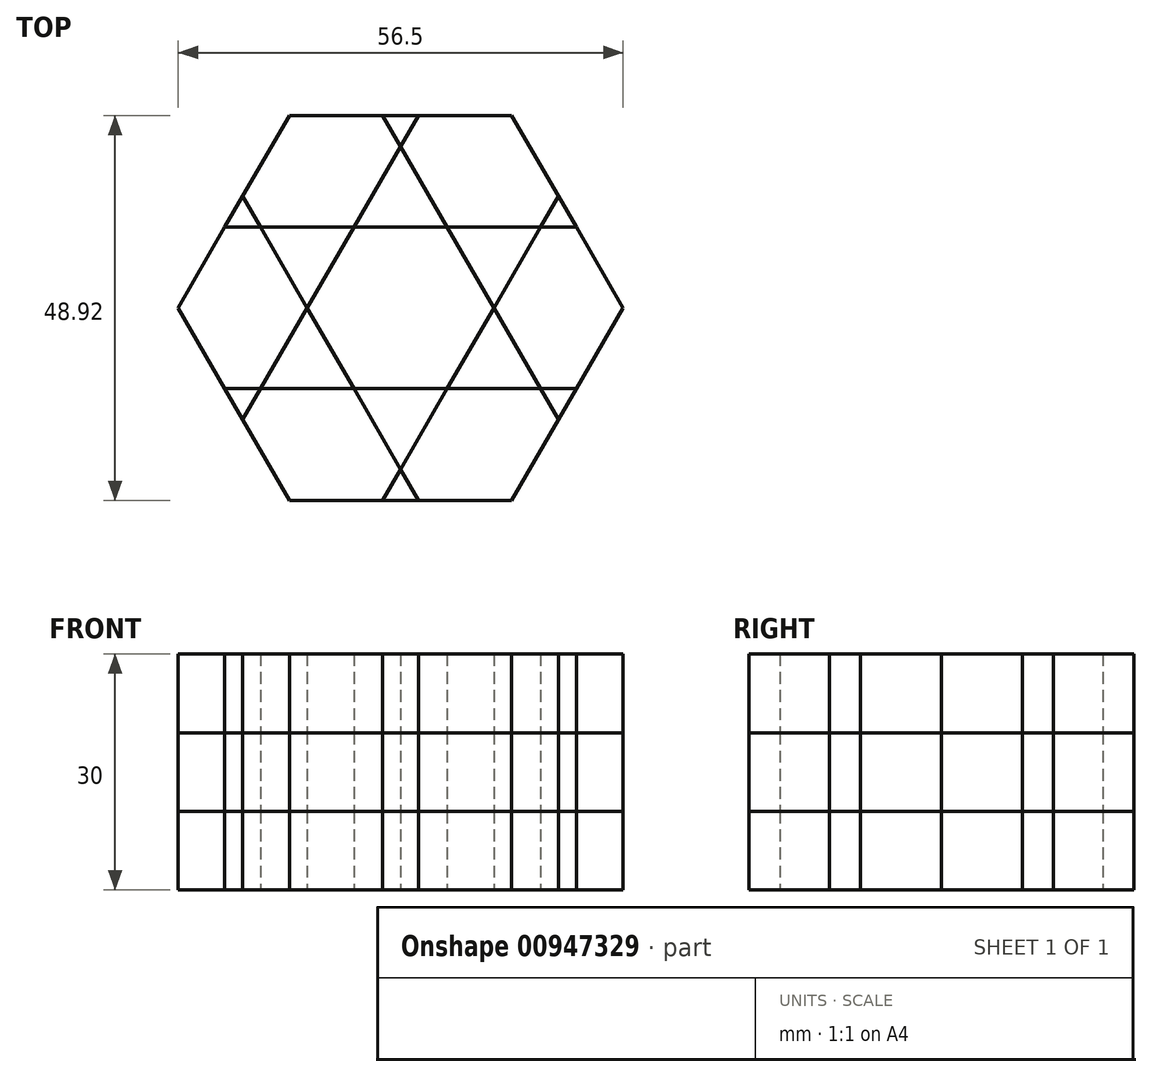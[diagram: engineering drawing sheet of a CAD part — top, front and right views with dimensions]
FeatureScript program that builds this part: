
annotation { "Feature Type Name" : "Feature", "Feature Type Description" : "" }
export const myFeature = defineFeature(function(context is Context, id is Id, definition is map)
    precondition{}
    {
        {
            var Q0;
            Q0=qCreatedBy(makeId("Top.planeOp"),FACE);
            var sketch = newSketch(context, id + "F0", { "sketchPlane" : qUnion([Q0])});
            skCircle(sketch, "E0.cCircle", {"center": v(0, 0) * mm, "radius": 10.26 * mm, "construction": true});
            skLineSegment(sketch, "E0.0", {"start": v(-5.92, 10.26) * mm, "end": v(5.92, 10.26) * mm});
            skLineSegment(sketch, "E0.1", {"start": v(5.92, 10.26) * mm, "end": v(11.85, 0) * mm});
            skLineSegment(sketch, "E0.2", {"start": v(11.85, 0) * mm, "end": v(5.92, -10.26) * mm});
            skLineSegment(sketch, "E0.3", {"start": v(5.92, -10.26) * mm, "end": v(-5.92, -10.26) * mm});
            skLineSegment(sketch, "E0.4", {"start": v(-5.92, -10.26) * mm, "end": v(-11.85, 0) * mm});
            skLineSegment(sketch, "E0.5", {"start": v(-11.85, 0) * mm, "end": v(-5.92, 10.26) * mm});
            skPoint(sketch, "E0.0.midPoint", {"position": v(0, 10.26) * mm});
            skCircle(sketch, "E1.cCircle", {"center": v(0, 0) * mm, "radius": 24.46 * mm, "construction": true});
            skLineSegment(sketch, "E1.0", {"start": v(-14.12, 24.46) * mm, "end": v(14.12, 24.46) * mm});
            skLineSegment(sketch, "E1.1", {"start": v(14.12, 24.46) * mm, "end": v(28.25, 0) * mm});
            skLineSegment(sketch, "E1.2", {"start": v(28.25, 0) * mm, "end": v(14.12, -24.46) * mm});
            skLineSegment(sketch, "E1.3", {"start": v(14.12, -24.46) * mm, "end": v(-14.12, -24.46) * mm});
            skLineSegment(sketch, "E1.4", {"start": v(-14.12, -24.46) * mm, "end": v(-28.25, 0) * mm});
            skLineSegment(sketch, "E1.5", {"start": v(-28.25, 0) * mm, "end": v(-14.12, 24.46) * mm});
            skPoint(sketch, "E1.0.midPoint", {"position": v(0, 24.46) * mm});
            skLineSegment(sketch, "E2", {"start": v(5.92, 10.26) * mm, "end": v(-2.28, 24.46) * mm});
            skLineSegment(sketch, "E3", {"start": v(5.92, -10.26) * mm, "end": v(22.32, -10.26) * mm});
            skLineSegment(sketch, "E4", {"start": v(11.85, 0) * mm, "end": v(20.05, 14.2) * mm});
            skLineSegment(sketch, "E5", {"start": v(-5.92, 10.26) * mm, "end": v(22.32, 10.26) * mm});
            skLineSegment(sketch, "E6", {"start": v(-5.92, 10.26) * mm, "end": v(-22.32, 10.26) * mm});
            skLineSegment(sketch, "E7", {"start": v(-5.92, 10.26) * mm, "end": v(2.28, 24.46) * mm});
            skLineSegment(sketch, "E8", {"start": v(-11.85, 0) * mm, "end": v(-20.05, 14.2) * mm});
            skLineSegment(sketch, "E9", {"start": v(-11.85, 0) * mm, "end": v(-20.05, -14.2) * mm});
            skLineSegment(sketch, "E10", {"start": v(-5.92, -10.26) * mm, "end": v(-22.32, -10.26) * mm});
            skLineSegment(sketch, "E11", {"start": v(5.92, -10.26) * mm, "end": v(-2.28, -24.46) * mm});
            skLineSegment(sketch, "E12", {"start": v(-5.92, -10.26) * mm, "end": v(2.28, -24.46) * mm});
            skLineSegment(sketch, "E13", {"start": v(11.85, 0) * mm, "end": v(20.05, -14.2) * mm});
            skSolve(sketch);
        }
        {
            var Q0;
            {var subQ5=sQuery(id+"F0.wireOp",EDGE,"E1.5");var subQ6=sQuery(id+"F0.wireOp",EDGE,"E1.0");var subQ7=makeQuery(id+"F0.imprint","INTERSECT",VERTEX,{"derivedFrom":[subQ6,subQ5]});Q0=makeQuery(id+"F0.imprint","IMPRINT",FACE,{"disambiguationData":[TD([[makeQuery(id+"F0.imprint","IMPRINT",EDGE,{"disambiguationData":[TD([[subQ7,-1.0]])],"derivedFrom":subQ6}),-1.0]])]});}
            var Q1;
            {var subQ0=sQuery(id+"F0.wireOp",EDGE,"E1.1");var subQ1=sQuery(id+"F0.wireOp",EDGE,"E1.0");var subQ2=makeQuery(id+"F0.imprint","INTERSECT",VERTEX,{"derivedFrom":[subQ1,subQ0]});Q1=makeQuery(id+"F0.imprint","IMPRINT",FACE,{"disambiguationData":[TD([[makeQuery(id+"F0.imprint","IMPRINT",EDGE,{"disambiguationData":[TD([[subQ2,1.0]])],"derivedFrom":subQ1}),-1.0]])]});}
            var Q2;
            {var subQ5=sQuery(id+"F0.wireOp",EDGE,"E1.2");var subQ6=sQuery(id+"F0.wireOp",EDGE,"E1.1");var subQ7=makeQuery(id+"F0.imprint","INTERSECT",VERTEX,{"derivedFrom":[subQ6,subQ5]});Q2=makeQuery(id+"F0.imprint","IMPRINT",FACE,{"disambiguationData":[TD([[makeQuery(id+"F0.imprint","IMPRINT",EDGE,{"disambiguationData":[TD([[subQ7,1.0]])],"derivedFrom":subQ6}),-1.0]])]});}
            var Q3;
            {var subQ1=sQuery(id+"F0.wireOp",EDGE,"E1.4");var subQ5=sQuery(id+"F0.wireOp",EDGE,"E1.3");var subQ6=makeQuery(id+"F0.imprint","INTERSECT",VERTEX,{"derivedFrom":[subQ5,subQ1]});Q3=makeQuery(id+"F0.imprint","IMPRINT",FACE,{"disambiguationData":[TD([[makeQuery(id+"F0.imprint","IMPRINT",EDGE,{"disambiguationData":[TD([[subQ6,1.0]])],"derivedFrom":subQ5}),-1.0]])]});}
            var Q4;
            {var subQ5=sQuery(id+"F0.wireOp",EDGE,"E1.5");var subQ6=sQuery(id+"F0.wireOp",EDGE,"E1.4");var subQ7=makeQuery(id+"F0.imprint","INTERSECT",VERTEX,{"derivedFrom":[subQ6,subQ5]});Q4=makeQuery(id+"F0.imprint","IMPRINT",FACE,{"disambiguationData":[TD([[makeQuery(id+"F0.imprint","IMPRINT",EDGE,{"disambiguationData":[TD([[subQ7,1.0]])],"derivedFrom":subQ6}),-1.0]])]});}
            var Q5;
            {var subQ7=sQuery(id+"F0.wireOp",EDGE,"E1.3");var subQ8=sQuery(id+"F0.wireOp",EDGE,"E1.2");var subQ9=makeQuery(id+"F0.imprint","INTERSECT",VERTEX,{"derivedFrom":[subQ8,subQ7]});Q5=makeQuery(id+"F0.imprint","IMPRINT",FACE,{"disambiguationData":[TD([[makeQuery(id+"F0.imprint","IMPRINT",EDGE,{"disambiguationData":[TD([[subQ9,1.0]])],"derivedFrom":subQ8}),-1.0]])]});}
            var Q6;
            {var subQ0=sQuery(id+"F0.wireOp",EDGE,"E0.1");Q6=makeQuery(id+"F0.imprint","IMPRINT",FACE,{"disambiguationData":[TD([[makeQuery(id+"F0.imprint","IMPRINT",EDGE,{"derivedFrom":subQ0}),-1.0]])]});}
            extrude(context, id + "F1", {"entities" : qUnion([Q0, Q1, Q2, Q3, Q4, Q5, Q6]), "depth" : 10 * mm, "offsetDistance" : 25.4 * mm});
        }
        {
            var Q0;
            {var subQ0=sQuery(id+"F0.wireOp",EDGE,"E6");var subQ1=sQuery(id+"F0.wireOp",EDGE,"E1.5");var subQ2=makeQuery(id+"F0.imprint","INTERSECT",VERTEX,{"derivedFrom":[subQ1,subQ0]});Q0=makeQuery(id+"F0.imprint","IMPRINT",FACE,{"disambiguationData":[TD([[makeQuery(id+"F0.imprint","IMPRINT",EDGE,{"disambiguationData":[TD([[subQ2,-1.0]])],"derivedFrom":subQ1}),-1.0]])]});}
            var Q1;
            {var subQ0=sQuery(id+"F0.wireOp",EDGE,"E0.5");Q1=makeQuery(id+"F0.imprint","IMPRINT",FACE,{"disambiguationData":[TD([[makeQuery(id+"F0.imprint","IMPRINT",EDGE,{"derivedFrom":subQ0}),1.0]])]});}
            var Q2;
            {var subQ0=sQuery(id+"F0.wireOp",EDGE,"E2");var subQ1=sQuery(id+"F0.wireOp",EDGE,"E1.0");var subQ2=makeQuery(id+"F0.imprint","INTERSECT",VERTEX,{"derivedFrom":[subQ1,subQ0]});Q2=makeQuery(id+"F0.imprint","IMPRINT",FACE,{"disambiguationData":[TD([[makeQuery(id+"F0.imprint","IMPRINT",EDGE,{"disambiguationData":[TD([[subQ2,-1.0]])],"derivedFrom":subQ1}),-1.0]])]});}
            var Q3;
            {var subQ1=sQuery(id+"F0.wireOp",EDGE,"E2");var subQ3=sQuery(id+"F0.wireOp",EDGE,"E7");var subQ4=makeQuery(id+"F0.imprint","INTERSECT",VERTEX,{"derivedFrom":[subQ1,subQ3]});Q3=makeQuery(id+"F0.imprint","IMPRINT",FACE,{"disambiguationData":[TD([[makeQuery(id+"F0.imprint","IMPRINT",EDGE,{"disambiguationData":[TD([[subQ4,1.0]])],"derivedFrom":subQ1}),1.0]])]});}
            var Q4;
            {var subQ0=sQuery(id+"F0.wireOp",EDGE,"E0.1");Q4=makeQuery(id+"F0.imprint","IMPRINT",FACE,{"disambiguationData":[TD([[makeQuery(id+"F0.imprint","IMPRINT",EDGE,{"derivedFrom":subQ0}),1.0]])]});}
            var Q5;
            {var subQ0=sQuery(id+"F0.wireOp",EDGE,"E4");var subQ1=sQuery(id+"F0.wireOp",EDGE,"E1.1");var subQ2=makeQuery(id+"F0.imprint","INTERSECT",VERTEX,{"derivedFrom":[subQ1,subQ0]});Q5=makeQuery(id+"F0.imprint","IMPRINT",FACE,{"disambiguationData":[TD([[makeQuery(id+"F0.imprint","IMPRINT",EDGE,{"disambiguationData":[TD([[subQ2,-1.0]])],"derivedFrom":subQ1}),-1.0]])]});}
            var Q6;
            {var subQ0=sQuery(id+"F0.wireOp",EDGE,"E0.2");Q6=makeQuery(id+"F0.imprint","IMPRINT",FACE,{"disambiguationData":[TD([[makeQuery(id+"F0.imprint","IMPRINT",EDGE,{"derivedFrom":subQ0}),1.0]])]});}
            var Q7;
            {var subQ0=sQuery(id+"F0.wireOp",EDGE,"E3");var subQ1=sQuery(id+"F0.wireOp",EDGE,"E1.2");var subQ2=makeQuery(id+"F0.imprint","INTERSECT",VERTEX,{"derivedFrom":[subQ1,subQ0]});Q7=makeQuery(id+"F0.imprint","IMPRINT",FACE,{"disambiguationData":[TD([[makeQuery(id+"F0.imprint","IMPRINT",EDGE,{"disambiguationData":[TD([[subQ2,-1.0]])],"derivedFrom":subQ1}),-1.0]])]});}
            var Q8;
            {var subQ0=sQuery(id+"F0.wireOp",EDGE,"E0.3");Q8=makeQuery(id+"F0.imprint","IMPRINT",FACE,{"disambiguationData":[TD([[makeQuery(id+"F0.imprint","IMPRINT",EDGE,{"derivedFrom":subQ0}),1.0]])]});}
            var Q9;
            {var subQ0=sQuery(id+"F0.wireOp",EDGE,"E0.4");Q9=makeQuery(id+"F0.imprint","IMPRINT",FACE,{"disambiguationData":[TD([[makeQuery(id+"F0.imprint","IMPRINT",EDGE,{"derivedFrom":subQ0}),1.0]])]});}
            var Q10;
            {var subQ0=sQuery(id+"F0.wireOp",EDGE,"E9");var subQ1=sQuery(id+"F0.wireOp",EDGE,"E1.4");var subQ2=makeQuery(id+"F0.imprint","INTERSECT",VERTEX,{"derivedFrom":[subQ1,subQ0]});Q10=makeQuery(id+"F0.imprint","IMPRINT",FACE,{"disambiguationData":[TD([[makeQuery(id+"F0.imprint","IMPRINT",EDGE,{"disambiguationData":[TD([[subQ2,-1.0]])],"derivedFrom":subQ1}),-1.0]])]});}
            var Q11;
            {var subQ0=sQuery(id+"F0.wireOp",EDGE,"E11");var subQ1=sQuery(id+"F0.wireOp",EDGE,"E1.3");var subQ2=makeQuery(id+"F0.imprint","INTERSECT",VERTEX,{"derivedFrom":[subQ1,subQ0]});Q11=makeQuery(id+"F0.imprint","IMPRINT",FACE,{"disambiguationData":[TD([[makeQuery(id+"F0.imprint","IMPRINT",EDGE,{"disambiguationData":[TD([[subQ2,1.0]])],"derivedFrom":subQ1}),-1.0]])]});}
            extrude(context, id + "F2", {"entities" : qUnion([Q0, Q1, Q2, Q3, Q4, Q5, Q6, Q7, Q8, Q9, Q10, Q11]), "depth" : 10 * mm, "offsetDistance" : 25.4 * mm});
        }
        {
            var Q0;
            Q0=makeQuery(id+"F1.opExtrude","SWEPT_BODY",BODY,{"disambiguationData":[OSD([sQuery(id+"F0.wireOp",EDGE,"E1.0"),sQuery(id+"F0.wireOp",EDGE,"E1.5"),sQuery(id+"F0.wireOp",EDGE,"E2"),sQuery(id+"F0.wireOp",EDGE,"E6"),sQuery(id+"F0.wireOp",EDGE,"E7"),sQuery(id+"F0.wireOp",EDGE,"E8")])]});
            var Q1;
            Q1=makeQuery(id+"F1.opExtrude","SWEPT_BODY",BODY,{"disambiguationData":[OSD([sQuery(id+"F0.wireOp",EDGE,"E1.0"),sQuery(id+"F0.wireOp",EDGE,"E1.1"),sQuery(id+"F0.wireOp",EDGE,"E2"),sQuery(id+"F0.wireOp",EDGE,"E4"),sQuery(id+"F0.wireOp",EDGE,"E5"),sQuery(id+"F0.wireOp",EDGE,"E7")])]});
            var Q2;
            Q2=makeQuery(id+"F1.opExtrude","SWEPT_BODY",BODY,{"disambiguationData":[OSD([sQuery(id+"F0.wireOp",EDGE,"E1.1"),sQuery(id+"F0.wireOp",EDGE,"E1.2"),sQuery(id+"F0.wireOp",EDGE,"E3"),sQuery(id+"F0.wireOp",EDGE,"E4"),sQuery(id+"F0.wireOp",EDGE,"E5"),sQuery(id+"F0.wireOp",EDGE,"E13")])]});
            var Q3;
            Q3=makeQuery(id+"F1.opExtrude","SWEPT_BODY",BODY,{"disambiguationData":[OSD([sQuery(id+"F0.wireOp",EDGE,"E1.2"),sQuery(id+"F0.wireOp",EDGE,"E1.3"),sQuery(id+"F0.wireOp",EDGE,"E3"),sQuery(id+"F0.wireOp",EDGE,"E11"),sQuery(id+"F0.wireOp",EDGE,"E12"),sQuery(id+"F0.wireOp",EDGE,"E13")])]});
            var Q4;
            Q4=makeQuery(id+"F1.opExtrude","SWEPT_BODY",BODY,{"disambiguationData":[OSD([sQuery(id+"F0.wireOp",EDGE,"E1.3"),sQuery(id+"F0.wireOp",EDGE,"E1.4"),sQuery(id+"F0.wireOp",EDGE,"E9"),sQuery(id+"F0.wireOp",EDGE,"E10"),sQuery(id+"F0.wireOp",EDGE,"E11"),sQuery(id+"F0.wireOp",EDGE,"E12")])]});
            var Q5;
            Q5=makeQuery(id+"F1.opExtrude","SWEPT_BODY",BODY,{"disambiguationData":[OSD([sQuery(id+"F0.wireOp",EDGE,"E1.4"),sQuery(id+"F0.wireOp",EDGE,"E1.5"),sQuery(id+"F0.wireOp",EDGE,"E6"),sQuery(id+"F0.wireOp",EDGE,"E8"),sQuery(id+"F0.wireOp",EDGE,"E9"),sQuery(id+"F0.wireOp",EDGE,"E10")])]});
            var Q6;
            Q6=makeQuery(id+"F2.opExtrude","SWEPT_BODY",BODY,{"disambiguationData":[OSD([sQuery(id+"F0.wireOp",EDGE,"E0.1"),sQuery(id+"F0.wireOp",EDGE,"E4"),sQuery(id+"F0.wireOp",EDGE,"E5")])]});
            var Q7;
            Q7=makeQuery(id+"F2.opExtrude","SWEPT_BODY",BODY,{"disambiguationData":[OSD([sQuery(id+"F0.wireOp",EDGE,"E0.2"),sQuery(id+"F0.wireOp",EDGE,"E3"),sQuery(id+"F0.wireOp",EDGE,"E13")])]});
            var Q8;
            Q8=makeQuery(id+"F2.opExtrude","SWEPT_BODY",BODY,{"disambiguationData":[OSD([sQuery(id+"F0.wireOp",EDGE,"E0.3"),sQuery(id+"F0.wireOp",EDGE,"E11"),sQuery(id+"F0.wireOp",EDGE,"E12")])]});
            var Q9;
            Q9=makeQuery(id+"F2.opExtrude","SWEPT_BODY",BODY,{"disambiguationData":[OSD([sQuery(id+"F0.wireOp",EDGE,"E0.4"),sQuery(id+"F0.wireOp",EDGE,"E9"),sQuery(id+"F0.wireOp",EDGE,"E10")])]});
            var Q10;
            Q10=makeQuery(id+"F2.opExtrude","SWEPT_BODY",BODY,{"disambiguationData":[OSD([sQuery(id+"F0.wireOp",EDGE,"E0.5"),sQuery(id+"F0.wireOp",EDGE,"E6"),sQuery(id+"F0.wireOp",EDGE,"E8")])]});
            var Q11;
            Q11=makeQuery(id+"F2.opExtrude","SWEPT_BODY",BODY,{"disambiguationData":[OSD([sQuery(id+"F0.wireOp",EDGE,"E1.0"),sQuery(id+"F0.wireOp",EDGE,"E2"),sQuery(id+"F0.wireOp",EDGE,"E7")])]});
            var Q12;
            Q12=makeQuery(id+"F2.opExtrude","SWEPT_BODY",BODY,{"disambiguationData":[OSD([sQuery(id+"F0.wireOp",EDGE,"E1.1"),sQuery(id+"F0.wireOp",EDGE,"E4"),sQuery(id+"F0.wireOp",EDGE,"E5")])]});
            var Q13;
            Q13=makeQuery(id+"F2.opExtrude","SWEPT_BODY",BODY,{"disambiguationData":[OSD([sQuery(id+"F0.wireOp",EDGE,"E1.2"),sQuery(id+"F0.wireOp",EDGE,"E3"),sQuery(id+"F0.wireOp",EDGE,"E13")])]});
            var Q14;
            Q14=makeQuery(id+"F2.opExtrude","SWEPT_BODY",BODY,{"disambiguationData":[OSD([sQuery(id+"F0.wireOp",EDGE,"E1.3"),sQuery(id+"F0.wireOp",EDGE,"E11"),sQuery(id+"F0.wireOp",EDGE,"E12")])]});
            var Q15;
            Q15=makeQuery(id+"F2.opExtrude","SWEPT_BODY",BODY,{"disambiguationData":[OSD([sQuery(id+"F0.wireOp",EDGE,"E1.4"),sQuery(id+"F0.wireOp",EDGE,"E9"),sQuery(id+"F0.wireOp",EDGE,"E10")])]});
            var Q16;
            Q16=makeQuery(id+"F2.opExtrude","SWEPT_BODY",BODY,{"disambiguationData":[OSD([sQuery(id+"F0.wireOp",EDGE,"E1.5"),sQuery(id+"F0.wireOp",EDGE,"E6"),sQuery(id+"F0.wireOp",EDGE,"E8")])]});
            var Q17;
            Q17=makeQuery(id+"F2.opExtrude","SWEPT_BODY",BODY,{"disambiguationData":[OSD([sQuery(id+"F0.wireOp",EDGE,"E2"),sQuery(id+"F0.wireOp",EDGE,"E5"),sQuery(id+"F0.wireOp",EDGE,"E7")])]});
            var Q18;
            Q18=makeQuery(id+"F1.opExtrude","SWEPT_BODY",BODY,{"disambiguationData":[OSD([sQuery(id+"F0.wireOp",EDGE,"E0.1"),sQuery(id+"F0.wireOp",EDGE,"E0.2"),sQuery(id+"F0.wireOp",EDGE,"E0.3"),sQuery(id+"F0.wireOp",EDGE,"E0.4"),sQuery(id+"F0.wireOp",EDGE,"E0.5"),sQuery(id+"F0.wireOp",EDGE,"E5")])]});
            transform(context, id + "F3", {"entities" : qUnion([Q0, Q1, Q2, Q3, Q4, Q5, Q6, Q7, Q8, Q9, Q10, Q11, Q12, Q13, Q14, Q15, Q16, Q17, Q18]), "transformType" : TransformType.TRANSLATION_3D, "dx" : 0 * mm, "dy" : 0 * mm, "dz" : 10 * mm, "makeCopy" : true});
        }
        {
            var Q0;
            Q0=makeQuery(id+"F1.opExtrude","SWEPT_BODY",BODY,{"disambiguationData":[OSD([sQuery(id+"F0.wireOp",EDGE,"E1.0"),sQuery(id+"F0.wireOp",EDGE,"E1.5"),sQuery(id+"F0.wireOp",EDGE,"E2"),sQuery(id+"F0.wireOp",EDGE,"E6"),sQuery(id+"F0.wireOp",EDGE,"E7"),sQuery(id+"F0.wireOp",EDGE,"E8")])]});
            var Q1;
            Q1=makeQuery(id+"F1.opExtrude","SWEPT_BODY",BODY,{"disambiguationData":[OSD([sQuery(id+"F0.wireOp",EDGE,"E1.0"),sQuery(id+"F0.wireOp",EDGE,"E1.1"),sQuery(id+"F0.wireOp",EDGE,"E2"),sQuery(id+"F0.wireOp",EDGE,"E4"),sQuery(id+"F0.wireOp",EDGE,"E5"),sQuery(id+"F0.wireOp",EDGE,"E7")])]});
            var Q2;
            Q2=makeQuery(id+"F1.opExtrude","SWEPT_BODY",BODY,{"disambiguationData":[OSD([sQuery(id+"F0.wireOp",EDGE,"E1.1"),sQuery(id+"F0.wireOp",EDGE,"E1.2"),sQuery(id+"F0.wireOp",EDGE,"E3"),sQuery(id+"F0.wireOp",EDGE,"E4"),sQuery(id+"F0.wireOp",EDGE,"E5"),sQuery(id+"F0.wireOp",EDGE,"E13")])]});
            var Q3;
            Q3=makeQuery(id+"F1.opExtrude","SWEPT_BODY",BODY,{"disambiguationData":[OSD([sQuery(id+"F0.wireOp",EDGE,"E1.2"),sQuery(id+"F0.wireOp",EDGE,"E1.3"),sQuery(id+"F0.wireOp",EDGE,"E3"),sQuery(id+"F0.wireOp",EDGE,"E11"),sQuery(id+"F0.wireOp",EDGE,"E12"),sQuery(id+"F0.wireOp",EDGE,"E13")])]});
            var Q4;
            Q4=makeQuery(id+"F1.opExtrude","SWEPT_BODY",BODY,{"disambiguationData":[OSD([sQuery(id+"F0.wireOp",EDGE,"E1.3"),sQuery(id+"F0.wireOp",EDGE,"E1.4"),sQuery(id+"F0.wireOp",EDGE,"E9"),sQuery(id+"F0.wireOp",EDGE,"E10"),sQuery(id+"F0.wireOp",EDGE,"E11"),sQuery(id+"F0.wireOp",EDGE,"E12")])]});
            var Q5;
            Q5=makeQuery(id+"F1.opExtrude","SWEPT_BODY",BODY,{"disambiguationData":[OSD([sQuery(id+"F0.wireOp",EDGE,"E1.4"),sQuery(id+"F0.wireOp",EDGE,"E1.5"),sQuery(id+"F0.wireOp",EDGE,"E6"),sQuery(id+"F0.wireOp",EDGE,"E8"),sQuery(id+"F0.wireOp",EDGE,"E9"),sQuery(id+"F0.wireOp",EDGE,"E10")])]});
            var Q6;
            Q6=makeQuery(id+"F2.opExtrude","SWEPT_BODY",BODY,{"disambiguationData":[OSD([sQuery(id+"F0.wireOp",EDGE,"E0.1"),sQuery(id+"F0.wireOp",EDGE,"E4"),sQuery(id+"F0.wireOp",EDGE,"E5")])]});
            var Q7;
            Q7=makeQuery(id+"F2.opExtrude","SWEPT_BODY",BODY,{"disambiguationData":[OSD([sQuery(id+"F0.wireOp",EDGE,"E0.2"),sQuery(id+"F0.wireOp",EDGE,"E3"),sQuery(id+"F0.wireOp",EDGE,"E13")])]});
            var Q8;
            Q8=makeQuery(id+"F2.opExtrude","SWEPT_BODY",BODY,{"disambiguationData":[OSD([sQuery(id+"F0.wireOp",EDGE,"E0.3"),sQuery(id+"F0.wireOp",EDGE,"E11"),sQuery(id+"F0.wireOp",EDGE,"E12")])]});
            var Q9;
            Q9=makeQuery(id+"F2.opExtrude","SWEPT_BODY",BODY,{"disambiguationData":[OSD([sQuery(id+"F0.wireOp",EDGE,"E0.4"),sQuery(id+"F0.wireOp",EDGE,"E9"),sQuery(id+"F0.wireOp",EDGE,"E10")])]});
            var Q10;
            Q10=makeQuery(id+"F2.opExtrude","SWEPT_BODY",BODY,{"disambiguationData":[OSD([sQuery(id+"F0.wireOp",EDGE,"E0.5"),sQuery(id+"F0.wireOp",EDGE,"E6"),sQuery(id+"F0.wireOp",EDGE,"E8")])]});
            var Q11;
            Q11=makeQuery(id+"F2.opExtrude","SWEPT_BODY",BODY,{"disambiguationData":[OSD([sQuery(id+"F0.wireOp",EDGE,"E1.0"),sQuery(id+"F0.wireOp",EDGE,"E2"),sQuery(id+"F0.wireOp",EDGE,"E7")])]});
            var Q12;
            Q12=makeQuery(id+"F2.opExtrude","SWEPT_BODY",BODY,{"disambiguationData":[OSD([sQuery(id+"F0.wireOp",EDGE,"E1.1"),sQuery(id+"F0.wireOp",EDGE,"E4"),sQuery(id+"F0.wireOp",EDGE,"E5")])]});
            var Q13;
            Q13=makeQuery(id+"F2.opExtrude","SWEPT_BODY",BODY,{"disambiguationData":[OSD([sQuery(id+"F0.wireOp",EDGE,"E1.2"),sQuery(id+"F0.wireOp",EDGE,"E3"),sQuery(id+"F0.wireOp",EDGE,"E13")])]});
            var Q14;
            Q14=makeQuery(id+"F2.opExtrude","SWEPT_BODY",BODY,{"disambiguationData":[OSD([sQuery(id+"F0.wireOp",EDGE,"E1.3"),sQuery(id+"F0.wireOp",EDGE,"E11"),sQuery(id+"F0.wireOp",EDGE,"E12")])]});
            var Q15;
            Q15=makeQuery(id+"F2.opExtrude","SWEPT_BODY",BODY,{"disambiguationData":[OSD([sQuery(id+"F0.wireOp",EDGE,"E1.4"),sQuery(id+"F0.wireOp",EDGE,"E9"),sQuery(id+"F0.wireOp",EDGE,"E10")])]});
            var Q16;
            Q16=makeQuery(id+"F1.opExtrude","SWEPT_BODY",BODY,{"disambiguationData":[OSD([sQuery(id+"F0.wireOp",EDGE,"E0.1"),sQuery(id+"F0.wireOp",EDGE,"E0.2"),sQuery(id+"F0.wireOp",EDGE,"E0.3"),sQuery(id+"F0.wireOp",EDGE,"E0.4"),sQuery(id+"F0.wireOp",EDGE,"E0.5"),sQuery(id+"F0.wireOp",EDGE,"E5")])]});
            var Q17;
            Q17=makeQuery(id+"F2.opExtrude","SWEPT_BODY",BODY,{"disambiguationData":[OSD([sQuery(id+"F0.wireOp",EDGE,"E1.5"),sQuery(id+"F0.wireOp",EDGE,"E6"),sQuery(id+"F0.wireOp",EDGE,"E8")])]});
            var Q18;
            Q18=makeQuery(id+"F2.opExtrude","SWEPT_BODY",BODY,{"disambiguationData":[OSD([sQuery(id+"F0.wireOp",EDGE,"E2"),sQuery(id+"F0.wireOp",EDGE,"E5"),sQuery(id+"F0.wireOp",EDGE,"E7")])]});
            transform(context, id + "F4", {"entities" : qUnion([Q0, Q1, Q2, Q3, Q4, Q5, Q6, Q7, Q8, Q9, Q10, Q11, Q12, Q13, Q14, Q15, Q16, Q17, Q18]), "transformType" : TransformType.TRANSLATION_3D, "dx" : 0 * mm, "dy" : 0 * mm, "dz" : 20 * mm, "makeCopy" : true});
        }
    });
